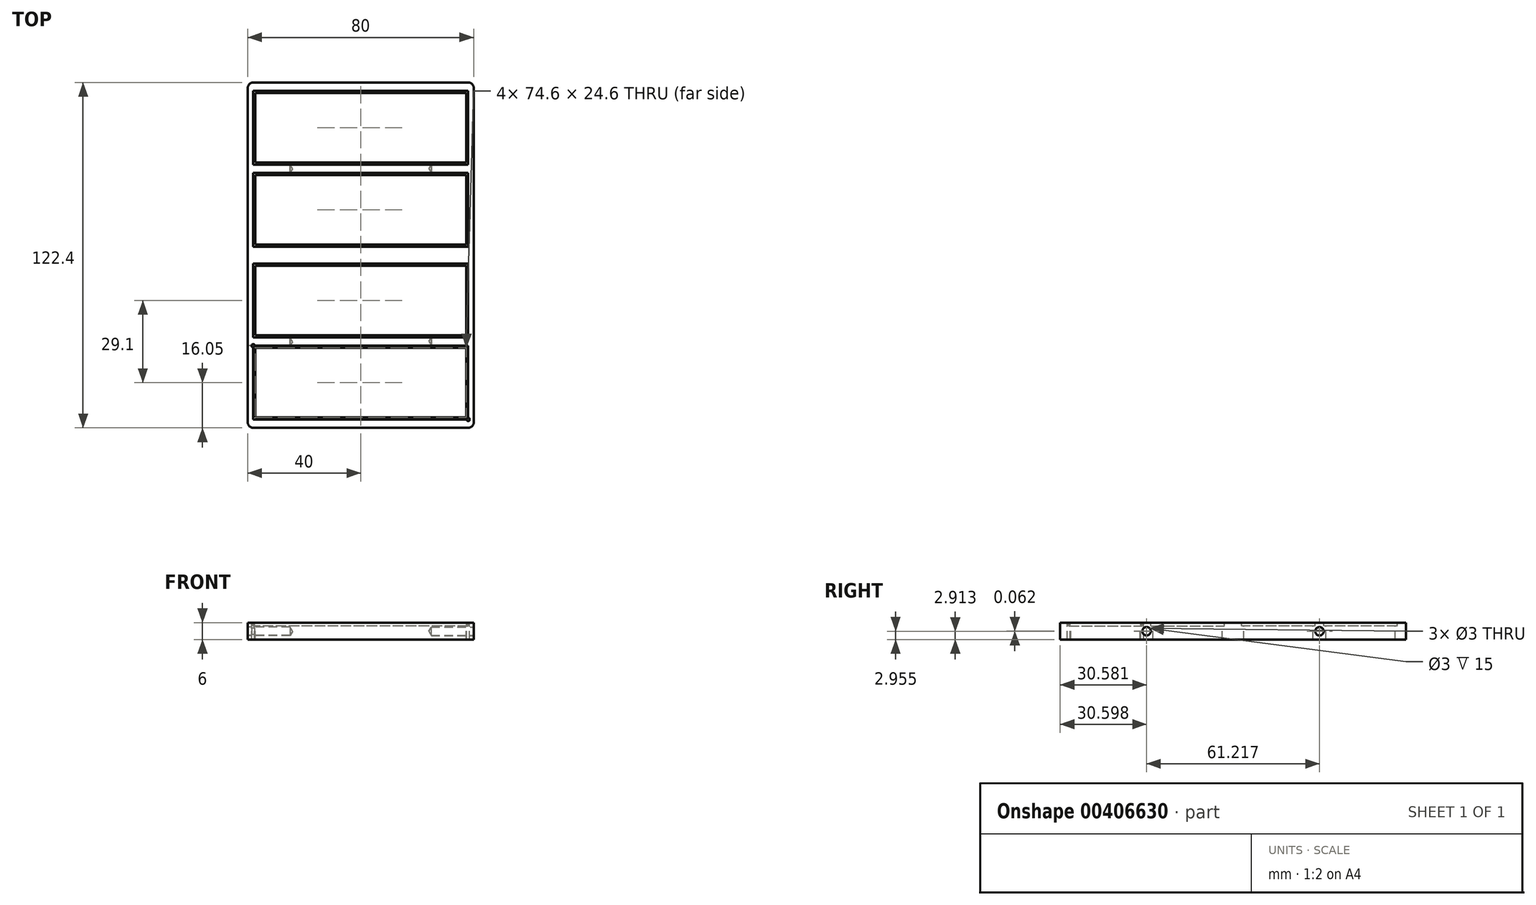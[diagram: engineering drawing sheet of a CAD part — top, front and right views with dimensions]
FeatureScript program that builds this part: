
annotation { "Feature Type Name" : "Feature", "Feature Type Description" : "" }
export const myFeature = defineFeature(function(context is Context, id is Id, definition is map)
    precondition{}
    {
        {
            var Q0;
            Q0=qCreatedBy(makeId("Top.planeOp"),FACE);
            var sketch = newSketch(context, id + "F0", { "sketchPlane" : qUnion([Q0])});
            skPoint(sketch, "E0.middle", {"position": v(0, 0) * mm});
            skLineSegment(sketch, "E1.bottom", {"start": v(40, -61.2) * mm, "end": v(-40, -61.2) * mm});
            skLineSegment(sketch, "E1.top", {"start": v(40, 61.2) * mm, "end": v(-40, 61.2) * mm});
            skLineSegment(sketch, "E1.left", {"start": v(40, -61.2) * mm, "end": v(40, 61.2) * mm});
            skLineSegment(sketch, "E1.right", {"start": v(-40, -61.2) * mm, "end": v(-40, 61.2) * mm});
            skSolve(sketch);
        }
        {
            var Q0;
            Q0 = qSketchRegion(id + "F0", true);
            extrude(context, id + "F1", {"entities" : qUnion([Q0]), "depth" : 6 * mm});
        }
        {
            var Q0;
            Q0=makeQuery(id+"F1.opExtrude","CAP_FACE",FACE,{"disambiguationData":[OSD([sQuery(id+"F0.wireOp",EDGE,"E1.bottom"),sQuery(id+"F0.wireOp",EDGE,"E1.top"),sQuery(id+"F0.wireOp",EDGE,"E1.left"),sQuery(id+"F0.wireOp",EDGE,"E1.right")])],"isStart":false});
            var sketch = newSketch(context, id + "F2", { "sketchPlane" : qUnion([Q0])});
            skLineSegment(sketch, "E2.bottom", {"start": v(38.05, -58.2) * mm, "end": v(-38.05, -58.2) * mm});
            skLineSegment(sketch, "E2.top", {"start": v(38.05, -32.1) * mm, "end": v(-38.05, -32.1) * mm});
            skLineSegment(sketch, "E2.left", {"start": v(38.05, -58.2) * mm, "end": v(38.05, -32.1) * mm});
            skLineSegment(sketch, "E2.right", {"start": v(-38.05, -58.2) * mm, "end": v(-38.05, -32.1) * mm});
            skPoint(sketch, "E2.middle", {"position": v(0, -45.15) * mm});
            skLineSegment(sketch, "E3.bottom", {"start": v(-38.05, -29.1) * mm, "end": v(38.05, -29.1) * mm});
            skLineSegment(sketch, "E3.top", {"start": v(-38.05, -3) * mm, "end": v(38.05, -3) * mm});
            skLineSegment(sketch, "E3.left", {"start": v(-38.05, -29.1) * mm, "end": v(-38.05, -3) * mm});
            skLineSegment(sketch, "E3.right", {"start": v(38.05, -29.1) * mm, "end": v(38.05, -3) * mm});
            skPoint(sketch, "E3.middle", {"position": v(0, -16.05) * mm});
            skLineSegment(sketch, "E4.MirrorCS", {"start": v(-38.05, 3) * mm, "end": v(38.05, 3) * mm});
            skLineSegment(sketch, "E5.MirrorCS", {"start": v(-38.05, 29.1) * mm, "end": v(-38.05, 3) * mm});
            skLineSegment(sketch, "E6.MirrorCS", {"start": v(-38.05, 29.1) * mm, "end": v(38.05, 29.1) * mm});
            skLineSegment(sketch, "E7.MirrorCS", {"start": v(38.05, 29.1) * mm, "end": v(38.05, 3) * mm});
            skLineSegment(sketch, "E8.MirrorCS", {"start": v(38.05, 32.1) * mm, "end": v(-38.05, 32.1) * mm});
            skLineSegment(sketch, "E9.MirrorCS", {"start": v(38.05, 58.2) * mm, "end": v(38.05, 32.1) * mm});
            skLineSegment(sketch, "E10.MirrorCS", {"start": v(38.05, 58.2) * mm, "end": v(-38.05, 58.2) * mm});
            skLineSegment(sketch, "E11.MirrorCS", {"start": v(-38.05, 58.2) * mm, "end": v(-38.05, 32.1) * mm});
            skLineSegment(sketch, "E12.bottom", {"start": v(37.3, -57.45) * mm, "end": v(-37.3, -57.45) * mm});
            skLineSegment(sketch, "E12.top", {"start": v(37.3, -32.85) * mm, "end": v(-37.3, -32.85) * mm});
            skLineSegment(sketch, "E12.left", {"start": v(37.3, -57.45) * mm, "end": v(37.3, -32.85) * mm});
            skLineSegment(sketch, "E12.right", {"start": v(-37.3, -57.45) * mm, "end": v(-37.3, -32.85) * mm});
            skLineSegment(sketch, "E13.bottom", {"start": v(37.3, -28.35) * mm, "end": v(-37.3, -28.35) * mm});
            skLineSegment(sketch, "E13.top", {"start": v(37.3, -3.75) * mm, "end": v(-37.3, -3.75) * mm});
            skLineSegment(sketch, "E13.left", {"start": v(37.3, -28.35) * mm, "end": v(37.3, -3.75) * mm});
            skLineSegment(sketch, "E13.right", {"start": v(-37.3, -28.35) * mm, "end": v(-37.3, -3.75) * mm});
            skLineSegment(sketch, "E14.MirrorCS", {"start": v(-37.3, 28.35) * mm, "end": v(-37.3, 3.75) * mm});
            skLineSegment(sketch, "E15.MirrorCS", {"start": v(37.3, 3.75) * mm, "end": v(-37.3, 3.75) * mm});
            skLineSegment(sketch, "E16.MirrorCS", {"start": v(37.3, 28.35) * mm, "end": v(-37.3, 28.35) * mm});
            skLineSegment(sketch, "E17.MirrorCS", {"start": v(37.3, 28.35) * mm, "end": v(37.3, 3.75) * mm});
            skLineSegment(sketch, "E18.MirrorCS", {"start": v(37.3, 32.85) * mm, "end": v(-37.3, 32.85) * mm});
            skLineSegment(sketch, "E19.MirrorCS", {"start": v(37.3, 57.45) * mm, "end": v(37.3, 32.85) * mm});
            skLineSegment(sketch, "E20.MirrorCS", {"start": v(37.3, 57.45) * mm, "end": v(-37.3, 57.45) * mm});
            skLineSegment(sketch, "E21.MirrorCS", {"start": v(-37.3, 57.45) * mm, "end": v(-37.3, 32.85) * mm});
            skSolve(sketch);
        }
        {
            var Q0;
            Q0=makeQuery(id+"F2.imprint","IMPRINT",FACE,{"disambiguationData":[TD([[makeQuery(id+"F2.imprint","IMPRINT",EDGE,{"derivedFrom":sQuery(id+"F2.wireOp",EDGE,"E2.bottom")}),-1.0]])]});
            var Q1;
            Q1=makeQuery(id+"F2.imprint","IMPRINT",FACE,{"disambiguationData":[TD([[makeQuery(id+"F2.imprint","IMPRINT",EDGE,{"derivedFrom":sQuery(id+"F2.wireOp",EDGE,"E3.bottom")}),1.0]])]});
            var Q2;
            Q2=makeQuery(id+"F2.imprint","IMPRINT",FACE,{"disambiguationData":[TD([[makeQuery(id+"F2.imprint","IMPRINT",EDGE,{"derivedFrom":sQuery(id+"F2.wireOp",EDGE,"E4.MirrorCS")}),1.0]])]});
            var Q3;
            Q3=makeQuery(id+"F2.imprint","IMPRINT",FACE,{"disambiguationData":[TD([[makeQuery(id+"F2.imprint","IMPRINT",EDGE,{"derivedFrom":sQuery(id+"F2.wireOp",EDGE,"E8.MirrorCS")}),-1.0]])]});
            extrude(context, id + "F3", {"entities" : qUnion([Q0, Q1, Q2, Q3]), "operationType" : NewBodyOperationType.REMOVE, "oppositeDirection" : true, "depth" : 1.2 * mm});
        }
        {
            var Q0;
            Q0=makeQuery(id+"F3.boolean.opBoolean","SPLIT",FACE,{"disambiguationData":[TD([makeQuery(id+"F3.opExtrude","SWEPT_FACE",FACE,{"disambiguationData":[OSD([sQuery(id+"F2.wireOp",EDGE,"E12.bottom")])]})])],"derivedFrom":makeQuery(id+"F1.opExtrude","CAP_FACE",FACE,{"disambiguationData":[OSD([sQuery(id+"F0.wireOp",EDGE,"E1.bottom"),sQuery(id+"F0.wireOp",EDGE,"E1.top"),sQuery(id+"F0.wireOp",EDGE,"E1.left"),sQuery(id+"F0.wireOp",EDGE,"E1.right")])],"isStart":false})});
            var Q1;
            Q1=makeQuery(id+"F3.boolean.opBoolean","SPLIT",FACE,{"disambiguationData":[TD([makeQuery(id+"F3.opExtrude","SWEPT_FACE",FACE,{"disambiguationData":[OSD([sQuery(id+"F2.wireOp",EDGE,"E13.bottom")])]})])],"derivedFrom":makeQuery(id+"F1.opExtrude","CAP_FACE",FACE,{"disambiguationData":[OSD([sQuery(id+"F0.wireOp",EDGE,"E1.bottom"),sQuery(id+"F0.wireOp",EDGE,"E1.top"),sQuery(id+"F0.wireOp",EDGE,"E1.left"),sQuery(id+"F0.wireOp",EDGE,"E1.right")])],"isStart":false})});
            var Q2;
            Q2=makeQuery(id+"F3.boolean.opBoolean","SPLIT",FACE,{"disambiguationData":[TD([makeQuery(id+"F3.opExtrude","SWEPT_FACE",FACE,{"disambiguationData":[OSD([sQuery(id+"F2.wireOp",EDGE,"E14.MirrorCS")])]})])],"derivedFrom":makeQuery(id+"F1.opExtrude","CAP_FACE",FACE,{"disambiguationData":[OSD([sQuery(id+"F0.wireOp",EDGE,"E1.bottom"),sQuery(id+"F0.wireOp",EDGE,"E1.top"),sQuery(id+"F0.wireOp",EDGE,"E1.left"),sQuery(id+"F0.wireOp",EDGE,"E1.right")])],"isStart":false})});
            var Q3;
            Q3=makeQuery(id+"F3.boolean.opBoolean","SPLIT",FACE,{"disambiguationData":[TD([makeQuery(id+"F3.opExtrude","SWEPT_FACE",FACE,{"disambiguationData":[OSD([sQuery(id+"F2.wireOp",EDGE,"E18.MirrorCS")])]})])],"derivedFrom":makeQuery(id+"F1.opExtrude","CAP_FACE",FACE,{"disambiguationData":[OSD([sQuery(id+"F0.wireOp",EDGE,"E1.bottom"),sQuery(id+"F0.wireOp",EDGE,"E1.top"),sQuery(id+"F0.wireOp",EDGE,"E1.left"),sQuery(id+"F0.wireOp",EDGE,"E1.right")])],"isStart":false})});
            extrude(context, id + "F4", {"entities" : qUnion([Q0, Q1, Q2, Q3]), "operationType" : NewBodyOperationType.REMOVE, "endBound" : BoundingType.THROUGH_ALL, "oppositeDirection" : true, "depth" : 25 * mm});
        }
        {
            var Q0;
            Q0=makeQuery(id+"F1.opExtrude","SWEPT_FACE",FACE,{"disambiguationData":[OSD([sQuery(id+"F0.wireOp",EDGE,"E1.left")])]});
            var sketch = newSketch(context, id + "F5", { "sketchPlane" : qUnion([Q0])});
            skLineSegment(sketch, "E22", {"start": v(-61.2, 3) * mm, "end": v(61.2, 2.9) * mm, "construction": true});
            skPoint(sketch, "E22.startSnap0", {"position": v(-61.2, 3) * mm});
            skLineSegment(sketch, "E23", {"start": v(-30.6, 6) * mm, "end": v(-30.6, 0) * mm, "construction": true});
            skPoint(sketch, "E24", {"position": v(-30.6, 2.97) * mm});
            skLineSegment(sketch, "E25", {"start": v(30.6, 6) * mm, "end": v(30.6, 0) * mm, "construction": true});
            skPoint(sketch, "E26", {"position": v(30.6, 2.92) * mm});
            skPoint(sketch, "E27", {"position": v(0, 2.95) * mm});
            skSolve(sketch);
        }
        {
            var Q0;
            Q0=sQuery(id+"F5.wireOp",VERTEX,"E24");
            var Q1;
            Q1=sQuery(id+"F5.wireOp",VERTEX,"E26");
            var Q2;
            Q2=makeQuery(id+"F1.opExtrude","SWEPT_BODY",BODY,{"disambiguationData":[OSD([sQuery(id+"F0.wireOp",EDGE,"E1.bottom"),sQuery(id+"F0.wireOp",EDGE,"E1.top"),sQuery(id+"F0.wireOp",EDGE,"E1.left"),sQuery(id+"F0.wireOp",EDGE,"E1.right")])]});
            hole(context, id + "F6", {"style" : HoleStyle.SIMPLE, "endStyle" : HoleEndStyle.BLIND, "holeDiameter" : 3 * mm, "holeDepth" : 15 * mm, "isTappedThrough" : true, "tappedDepth" : 12 * mm, "tapClearance" : 3, "startFromSketch" : true, "locations" : qUnion([Q0, Q1]), "scope" : qUnion([Q2])});
        }
        {
            var Q0;
            Q0=makeQuery(id+"F1.opExtrude","SWEPT_FACE",FACE,{"disambiguationData":[OSD([sQuery(id+"F0.wireOp",EDGE,"E1.right")])]});
            var sketch = newSketch(context, id + "F7", { "sketchPlane" : qUnion([Q0])});
            skPoint(sketch, "E28", {"position": v(-30.61, 2.91) * mm});
            skPoint(sketch, "E29", {"position": v(30.62, 2.96) * mm});
            skSolve(sketch);
        }
        {
            var Q0;
            Q0=sQuery(id+"F7.wireOp",VERTEX,"E29");
            var Q1;
            Q1=sQuery(id+"F7.wireOp",VERTEX,"E28");
            var Q2;
            Q2=makeQuery(id+"F1.opExtrude","SWEPT_BODY",BODY,{"disambiguationData":[OSD([sQuery(id+"F0.wireOp",EDGE,"E1.bottom"),sQuery(id+"F0.wireOp",EDGE,"E1.top"),sQuery(id+"F0.wireOp",EDGE,"E1.left"),sQuery(id+"F0.wireOp",EDGE,"E1.right")])]});
            hole(context, id + "F8", {"style" : HoleStyle.SIMPLE, "endStyle" : HoleEndStyle.BLIND, "holeDiameter" : 3 * mm, "holeDepth" : 15 * mm, "isTappedThrough" : true, "tappedDepth" : 12 * mm, "tapClearance" : 3, "startFromSketch" : true, "locations" : qUnion([Q0, Q1]), "scope" : qUnion([Q2])});
        }
        {
            var Q0;
            Q0=makeQuery(id+"F1.opExtrude","SWEPT_EDGE",EDGE,{"disambiguationData":[OSD([sQuery(id+"F0.wireOp",EDGE,"E1.bottom"),sQuery(id+"F0.wireOp",EDGE,"E1.right")])]});
            var Q1;
            Q1=makeQuery(id+"F1.opExtrude","SWEPT_EDGE",EDGE,{"disambiguationData":[OSD([sQuery(id+"F0.wireOp",EDGE,"E1.bottom"),sQuery(id+"F0.wireOp",EDGE,"E1.left")])]});
            var Q2;
            Q2=makeQuery(id+"F1.opExtrude","SWEPT_EDGE",EDGE,{"disambiguationData":[OSD([sQuery(id+"F0.wireOp",EDGE,"E1.top"),sQuery(id+"F0.wireOp",EDGE,"E1.left")])]});
            var Q3;
            Q3=makeQuery(id+"F1.opExtrude","SWEPT_EDGE",EDGE,{"disambiguationData":[OSD([sQuery(id+"F0.wireOp",EDGE,"E1.top"),sQuery(id+"F0.wireOp",EDGE,"E1.right")])]});
            fillet(context, id + "F9", {"entities" : qUnion([Q0, Q1, Q2, Q3]), "radius" : 2 * mm, "tangentPropagation" : true, "allowEdgeOverflow" : false});
        }
        {
            var Q0;
            {var subQ0=sQuery(id+"F0.wireOp",EDGE,"E1.left");var subQ1=sQuery(id+"F0.wireOp",EDGE,"E1.bottom");var subQ2=sQuery(id+"F0.wireOp",EDGE,"E1.right");var subQ3=sQuery(id+"F0.wireOp",EDGE,"E1.top");Q0=makeQuery(id+"F3.boolean.opBoolean","SPLIT",FACE,{"disambiguationData":[TD([makeQuery(id+"F1.opExtrude","SWEPT_FACE",FACE,{"disambiguationData":[OSD([subQ1])]})])],"derivedFrom":makeQuery(id+"F1.opExtrude","CAP_FACE",FACE,{"disambiguationData":[OSD([subQ1,subQ3,subQ0,subQ2])],"isStart":false})});}
            var sketch = newSketch(context, id + "F10", { "sketchPlane" : qUnion([Q0])});
            skLineSegment(sketch, "E30.bottom", {"start": v(-37.55, -32.6) * mm, "end": v(-38.3, -32.6) * mm});
            skLineSegment(sketch, "E30.top", {"start": v(-37.8, -31.6) * mm, "end": v(-38.3, -31.6) * mm});
            skLineSegment(sketch, "E30.left", {"start": v(-37.55, -32.6) * mm, "end": v(-37.55, -31.85) * mm});
            skLineSegment(sketch, "E30.right", {"start": v(-38.55, -32.35) * mm, "end": v(-38.55, -31.85) * mm});
            skPoint(sketch, "E30.middle", {"position": v(-38.05, -32.1) * mm});
            skPoint(sketch, "E31.visualSharp", {"position": v(-38.55, -32.6) * mm});
            skArc(sketch, "E31.filletArc", {"start": v(-38.55, -32.35) * mm, "mid": v(-38.48, -32.53) * mm, "end": v(-38.3, -32.6) * mm});
            skPoint(sketch, "E32.visualSharp", {"position": v(-38.55, -31.6) * mm});
            skArc(sketch, "E32.filletArc", {"start": v(-38.3, -31.6) * mm, "mid": v(-38.48, -31.67) * mm, "end": v(-38.55, -31.85) * mm});
            skPoint(sketch, "E33.visualSharp", {"position": v(-37.55, -31.6) * mm});
            skArc(sketch, "E33.filletArc", {"start": v(-37.55, -31.85) * mm, "mid": v(-37.62, -31.67) * mm, "end": v(-37.8, -31.6) * mm});
            skSolve(sketch);
        }
        {
            var Q0;
            Q0=makeQuery(id+"F10.imprint","IMPRINT",FACE,{"disambiguationData":[TD([[makeQuery(id+"F10.imprint","IMPRINT",EDGE,{"derivedFrom":sQuery(id+"F10.wireOp",EDGE,"E30.top")}),1.0]])]});
            extrude(context, id + "F11", {"entities" : qUnion([Q0]), "operationType" : NewBodyOperationType.REMOVE, "endBound" : BoundingType.THROUGH_ALL, "oppositeDirection" : true, "depth" : 25 * mm});
        }
        {
            var Q0;
            Q0=makeQuery(id+"F3.boolean.opBoolean","COPY",FACE,{"derivedFrom":makeQuery(id+"F3.opExtrude","CAP_FACE",FACE,{"disambiguationData":[OSD([sQuery(id+"F2.wireOp",EDGE,"E2.bottom"),sQuery(id+"F2.wireOp",EDGE,"E2.top"),sQuery(id+"F2.wireOp",EDGE,"E2.left"),sQuery(id+"F2.wireOp",EDGE,"E2.right"),sQuery(id+"F2.wireOp",EDGE,"E12.bottom"),sQuery(id+"F2.wireOp",EDGE,"E12.top"),sQuery(id+"F2.wireOp",EDGE,"E12.left"),sQuery(id+"F2.wireOp",EDGE,"E12.right")])],"isStart":false})});
            var sketch = newSketch(context, id + "F12", { "sketchPlane" : qUnion([Q0])});
            skLineSegment(sketch, "E34", {"start": v(-38.05, -32.6) * mm, "end": v(-37.55, -32.6) * mm});
            skLineSegment(sketch, "E35", {"start": v(-37.55, -32.6) * mm, "end": v(-37.55, -32.1) * mm});
            skSolve(sketch);
        }
        {
            var Q0;
            Q0=makeQuery(id+"F12.imprint","IMPRINT",FACE,{"disambiguationData":[TD([[makeQuery(id+"F12.imprint","IMPRINT",EDGE,{"derivedFrom":sQuery(id+"F12.wireOp",EDGE,"E34")}),1.0]])]});
            extrude(context, id + "F13", {"entities" : qUnion([Q0]), "operationType" : NewBodyOperationType.REMOVE, "endBound" : BoundingType.THROUGH_ALL, "oppositeDirection" : true, "depth" : 25 * mm});
        }
        {
            var Q0;
            {var subQ0=sQuery(id+"F0.wireOp",EDGE,"E1.left");var subQ1=sQuery(id+"F0.wireOp",EDGE,"E1.bottom");var subQ2=sQuery(id+"F0.wireOp",EDGE,"E1.right");var subQ3=sQuery(id+"F0.wireOp",EDGE,"E1.top");Q0=makeQuery(id+"F3.boolean.opBoolean","SPLIT",FACE,{"disambiguationData":[TD([makeQuery(id+"F1.opExtrude","SWEPT_FACE",FACE,{"disambiguationData":[OSD([subQ1])]})])],"derivedFrom":makeQuery(id+"F1.opExtrude","CAP_FACE",FACE,{"disambiguationData":[OSD([subQ1,subQ3,subQ0,subQ2])],"isStart":false})});}
            var sketch = newSketch(context, id + "F14", { "sketchPlane" : qUnion([Q0])});
            skLineSegment(sketch, "E36.bottom", {"start": v(38.3, -58.7) * mm, "end": v(37.8, -58.7) * mm});
            skLineSegment(sketch, "E36.top", {"start": v(38.3, -57.7) * mm, "end": v(37.55, -57.7) * mm});
            skLineSegment(sketch, "E36.left", {"start": v(38.55, -58.45) * mm, "end": v(38.55, -57.95) * mm});
            skLineSegment(sketch, "E36.right", {"start": v(37.55, -58.45) * mm, "end": v(37.55, -57.7) * mm});
            skPoint(sketch, "E36.middle", {"position": v(38.05, -58.2) * mm});
            skPoint(sketch, "E37.visualSharp", {"position": v(38.55, -57.7) * mm});
            skArc(sketch, "E37.filletArc", {"start": v(38.55, -57.95) * mm, "mid": v(38.48, -57.77) * mm, "end": v(38.3, -57.7) * mm});
            skPoint(sketch, "E38.visualSharp", {"position": v(38.55, -58.7) * mm});
            skArc(sketch, "E38.filletArc", {"start": v(38.3, -58.7) * mm, "mid": v(38.48, -58.63) * mm, "end": v(38.55, -58.45) * mm});
            skPoint(sketch, "E39.visualSharp", {"position": v(37.55, -58.7) * mm});
            skArc(sketch, "E39.filletArc", {"start": v(37.55, -58.45) * mm, "mid": v(37.62, -58.63) * mm, "end": v(37.8, -58.7) * mm});
            skSolve(sketch);
        }
        {
            var Q0;
            Q0=makeQuery(id+"F14.imprint","IMPRINT",FACE,{"disambiguationData":[TD([[makeQuery(id+"F14.imprint","IMPRINT",EDGE,{"derivedFrom":sQuery(id+"F14.wireOp",EDGE,"E36.bottom")}),-1.0]])]});
            extrude(context, id + "F15", {"entities" : qUnion([Q0]), "operationType" : NewBodyOperationType.REMOVE, "endBound" : BoundingType.THROUGH_ALL, "oppositeDirection" : true, "depth" : 25 * mm});
        }
        {
            var Q0;
            Q0=makeQuery(id+"F3.boolean.opBoolean","COPY",FACE,{"derivedFrom":makeQuery(id+"F3.opExtrude","CAP_FACE",FACE,{"disambiguationData":[OSD([sQuery(id+"F2.wireOp",EDGE,"E2.bottom"),sQuery(id+"F2.wireOp",EDGE,"E2.top"),sQuery(id+"F2.wireOp",EDGE,"E2.left"),sQuery(id+"F2.wireOp",EDGE,"E2.right"),sQuery(id+"F2.wireOp",EDGE,"E12.bottom"),sQuery(id+"F2.wireOp",EDGE,"E12.top"),sQuery(id+"F2.wireOp",EDGE,"E12.left"),sQuery(id+"F2.wireOp",EDGE,"E12.right")])],"isStart":false})});
            var sketch = newSketch(context, id + "F16", { "sketchPlane" : qUnion([Q0])});
            skLineSegment(sketch, "E40", {"start": v(37.55, -58.2) * mm, "end": v(37.55, -57.7) * mm});
            skLineSegment(sketch, "E41", {"start": v(37.55, -57.7) * mm, "end": v(38.05, -57.7) * mm});
            skSolve(sketch);
        }
        {
            var Q0;
            Q0=makeQuery(id+"F16.imprint","IMPRINT",FACE,{"disambiguationData":[TD([[makeQuery(id+"F16.imprint","IMPRINT",EDGE,{"derivedFrom":sQuery(id+"F16.wireOp",EDGE,"E40")}),-1.0]])]});
            extrude(context, id + "F17", {"entities" : qUnion([Q0]), "operationType" : NewBodyOperationType.REMOVE, "endBound" : BoundingType.THROUGH_ALL, "oppositeDirection" : true, "depth" : 25 * mm});
        }
        {
            var Q0;
            Q0=makeQuery(id+"F3.boolean.opBoolean","COPY",FACE,{"derivedFrom":makeQuery(id+"F3.opExtrude","CAP_FACE",FACE,{"disambiguationData":[OSD([sQuery(id+"F2.wireOp",EDGE,"E2.bottom"),sQuery(id+"F2.wireOp",EDGE,"E2.top"),sQuery(id+"F2.wireOp",EDGE,"E2.left"),sQuery(id+"F2.wireOp",EDGE,"E2.right"),sQuery(id+"F2.wireOp",EDGE,"E12.bottom"),sQuery(id+"F2.wireOp",EDGE,"E12.top"),sQuery(id+"F2.wireOp",EDGE,"E12.left"),sQuery(id+"F2.wireOp",EDGE,"E12.right")])],"isStart":false})});
            var sketch = newSketch(context, id + "F18", { "sketchPlane" : qUnion([Q0])});
            skArc(sketch, "E42", {"start": v(-37.49, -56.93) * mm, "mid": v(-36.85, -57.13) * mm, "end": v(-36.88, -57.8) * mm});
            skLineSegment(sketch, "E43", {"start": v(-37.49, -56.93) * mm, "end": v(-37.74, -56.93) * mm});
            skLineSegment(sketch, "E44", {"start": v(-37.74, -56.93) * mm, "end": v(-37.74, -54.93) * mm});
            skLineSegment(sketch, "E45", {"start": v(-36.88, -57.8) * mm, "end": v(-36.88, -58.05) * mm});
            skLineSegment(sketch, "E46", {"start": v(-36.88, -58.05) * mm, "end": v(-34.88, -58.05) * mm});
            skLineSegment(sketch, "E47.0", {"start": v(-37.79, -56.98) * mm, "end": v(-37.79, -54.93) * mm});
            skArc(sketch, "E48.0", {"start": v(-37.48, -56.98) * mm, "mid": v(-36.9, -57.16) * mm, "end": v(-36.92, -57.77) * mm});
            skLineSegment(sketch, "E49.2", {"start": v(-36.92, -57.77) * mm, "end": v(-36.92, -58.09) * mm});
            skLineSegment(sketch, "E49.3", {"start": v(-36.92, -58.09) * mm, "end": v(-34.88, -58.1) * mm});
            skLineSegment(sketch, "E50.0", {"start": v(-37.48, -56.98) * mm, "end": v(-37.79, -56.98) * mm});
            skLineSegment(sketch, "E51", {"start": v(-37.74, -54.93) * mm, "end": v(-37.79, -54.93) * mm});
            skLineSegment(sketch, "E52", {"start": v(-34.88, -58.05) * mm, "end": v(-34.88, -58.1) * mm});
            skSolve(sketch);
        }
        {
            var Q0;
            Q0=sQuery(id+"F18.wireOp",EDGE,"E42");
            var Q1;
            Q1=sQuery(id+"F18.wireOp",EDGE,"E45");
            var Q2;
            Q2=sQuery(id+"F18.wireOp",EDGE,"E46");
            var Q3;
            Q3=sQuery(id+"F18.wireOp",EDGE,"E49.3");
            var Q4;
            Q4=sQuery(id+"F18.wireOp",EDGE,"E43");
            var Q5;
            Q5=sQuery(id+"F18.wireOp",EDGE,"E50.0");
            var Q6;
            Q6=sQuery(id+"F18.wireOp",EDGE,"E47.0");
            var Q7;
            Q7=sQuery(id+"F18.wireOp",EDGE,"E44");
            var Q8;
            Q8=sQuery(id+"F18.wireOp",EDGE,"E52");
            var Q9;
            Q9=sQuery(id+"F18.wireOp",EDGE,"E51");
            var Q10;
            Q10=sQuery(id+"F18.wireOp",EDGE,"E48.0");
            var Q11;
            Q11=sQuery(id+"F18.wireOp",EDGE,"E49.2");
            extrude(context, id + "F19", {"bodyType" : ToolBodyType.SURFACE, "surfaceEntities" : qUnion([Q0, Q1, Q2, Q3, Q4, Q5, Q6, Q7, Q8, Q9, Q10, Q11]), "depth" : 1.5 * mm});
        }
    });
